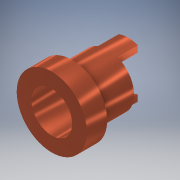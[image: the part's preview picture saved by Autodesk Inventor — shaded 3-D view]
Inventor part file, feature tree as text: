
AUTODESK INVENTOR PART (.ipt)
format: ipt  version: 2017 SP1 (Build 210196100, 196)  size: 142,848 bytes
history: native  units: mm
features: extrude x4, sketch x4, other x3, projected_geometry x2
ambient origin geometry x8: Origin, YZ Plane, XZ Plane, XY Plane, X Axis, Y Axis, Z Axis, Center Point
bodies: Body1 (feature_tree)
feature tree (13):
  other  "Bryła1"
  extrude  "Wyciągnięcie proste1"  Depth=13.75mm
  extrude  "Wyciągnięcie proste2"  Depth=8.0mm
  other  "Płaszczyzna konstrukcyjna1"
  extrude  "Wyciągnięcie proste3"  Depth=4.0mm TaperAngle=0.0deg
  other  "Płaszczyzna konstrukcyjna2"
  extrude  "Wyciągnięcie proste4"  Depth=10.3mm
  sketch  "Szkic1"
  sketch  "Szkic2"
  sketch  "Szkic3"
  projected_geometry  "Pętla rzutowana1"
  sketch  "Szkic4"
  projected_geometry  "Pętla rzutowana2"
